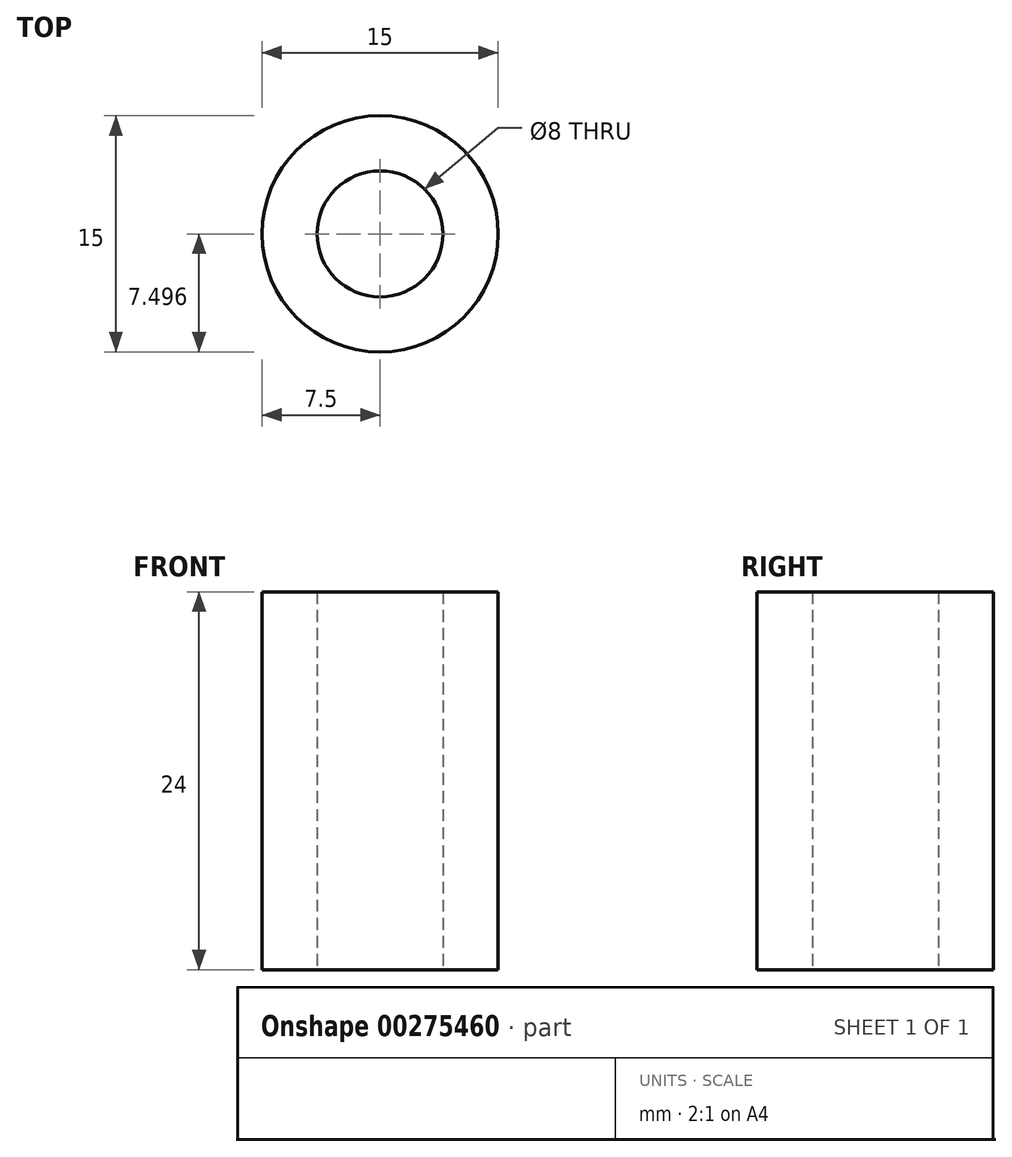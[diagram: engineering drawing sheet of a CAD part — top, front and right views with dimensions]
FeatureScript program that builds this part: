
annotation { "Feature Type Name" : "Feature", "Feature Type Description" : "" }
export const myFeature = defineFeature(function(context is Context, id is Id, definition is map)
    precondition{}
    {
        {
            var Q0;
            Q0=qCreatedBy(makeId("Top.planeOp"),FACE);
            var sketch = newSketch(context, id + "F0", { "sketchPlane" : qUnion([Q0])});
            skCircle(sketch, "E0", {"center": v(-39.51, 24.63) * mm, "radius": 7.5 * mm});
            skCircle(sketch, "E1", {"center": v(-39.51, 24.63) * mm, "radius": 4 * mm});
            skSolve(sketch);
        }
        {
            var Q0;
            Q0=qSketchRegion(id+"F0",true);
            extrude(context, id + "F1", {"entities" : qUnion([Q0]), "depth" : 24 * mm});
        }
    });
